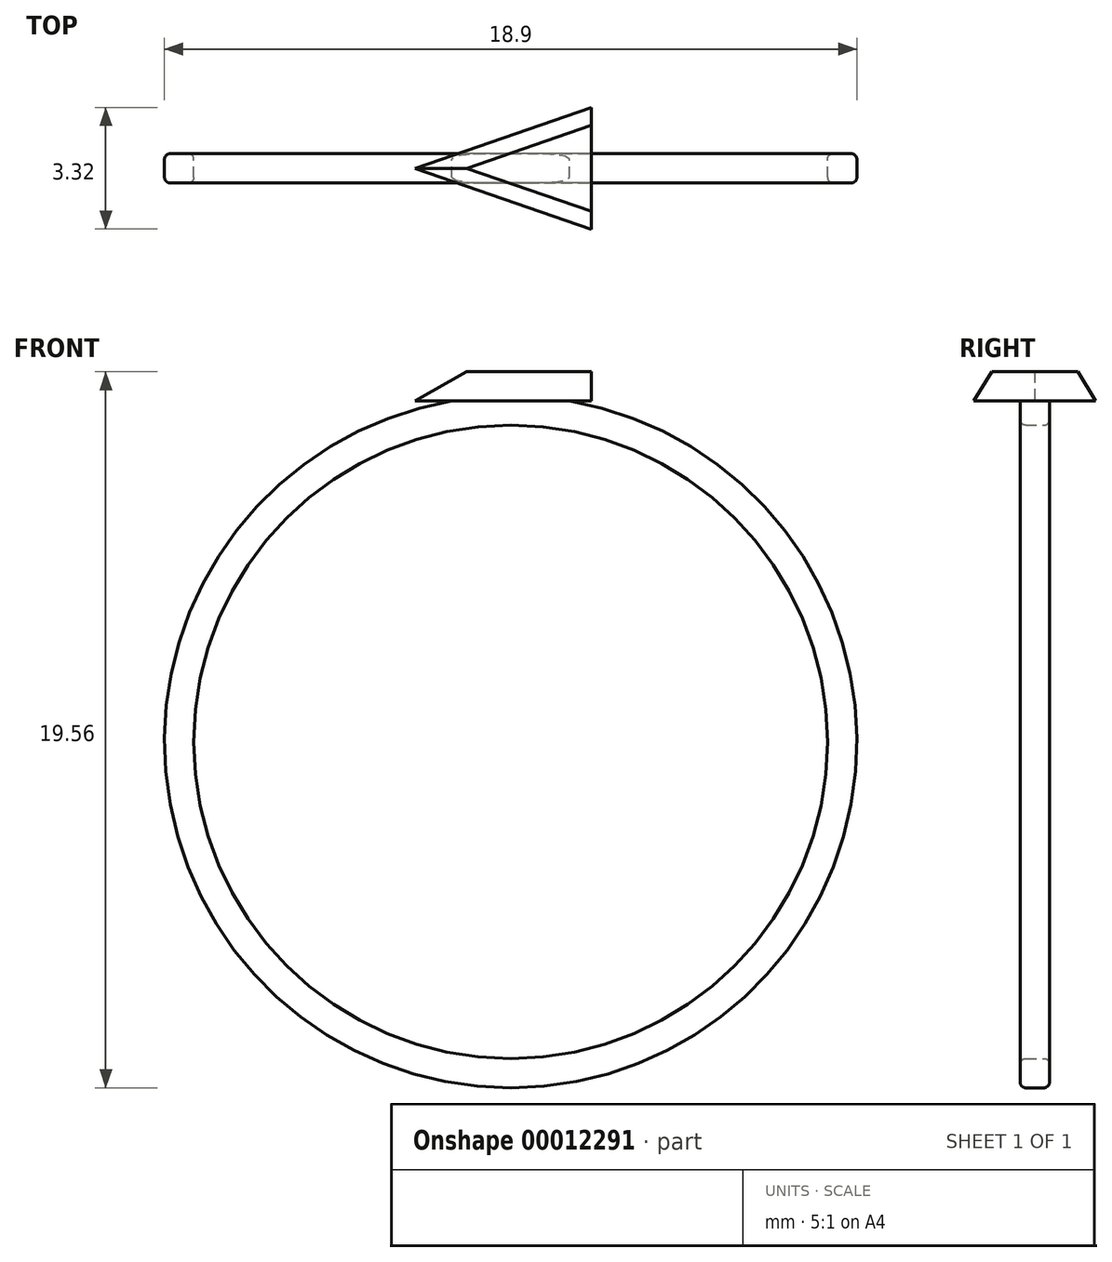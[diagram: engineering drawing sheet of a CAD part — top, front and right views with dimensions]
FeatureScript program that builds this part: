
annotation { "Feature Type Name" : "Feature", "Feature Type Description" : "" }
export const myFeature = defineFeature(function(context is Context, id is Id, definition is map)
    precondition{}
    {
        {
            var Q0;
            Q0=qCreatedBy(makeId("Front.planeOp"),FACE);
            var sketch = newSketch(context, id + "F0", { "sketchPlane" : qUnion([Q0])});
            skCircle(sketch, "E0", {"center": v(0, 0) * mm, "radius": 8.65 * mm});
            skCircle(sketch, "E1", {"center": v(0, 0) * mm, "radius": 9.45 * mm});
            skLineSegment(sketch, "E2", {"start": v(-1.6, 9.31) * mm, "end": v(1.6, 9.31) * mm});
            skLineSegment(sketch, "E3", {"start": v(1.6, 9.31) * mm, "end": v(0, 0) * mm});
            skLineSegment(sketch, "E4", {"start": v(-1.6, 9.31) * mm, "end": v(0, 0) * mm});
            skSolve(sketch);
        }
        {
            var Q0;
            {var subQ1=sQuery(id+"F0.wireOp",EDGE,"E0");var subQ6=sQuery(id+"F0.wireOp",EDGE,"E3");var subQ7=makeQuery(id+"F0.imprint","INTERSECT",VERTEX,{"derivedFrom":[subQ1,subQ6]});Q0=makeQuery(id+"F0.imprint","IMPRINT",FACE,{"disambiguationData":[TD([[makeQuery(id+"F0.imprint","IMPRINT",EDGE,{"disambiguationData":[TD([[subQ7,1.0]])],"derivedFrom":subQ1}),-1.0]])]});}
            var Q1;
            {var subQ4=sQuery(id+"F0.wireOp",EDGE,"E2");Q1=makeQuery(id+"F0.imprint","IMPRINT",FACE,{"disambiguationData":[TD([[makeQuery(id+"F0.imprint","IMPRINT",EDGE,{"derivedFrom":subQ4}),-1.0]])]});}
            extrude(context, id + "F1", {"entities" : qUnion([Q0, Q1]), "depth" : .4 * mm});
        }
        {
            var Q0;
            {var subQ1=sQuery(id+"F0.wireOp",EDGE,"E0");var subQ6=sQuery(id+"F0.wireOp",EDGE,"E3");var subQ7=makeQuery(id+"F0.imprint","INTERSECT",VERTEX,{"derivedFrom":[subQ1,subQ6]});Q0=makeQuery(id+"F0.imprint","IMPRINT",FACE,{"disambiguationData":[TD([[makeQuery(id+"F0.imprint","IMPRINT",EDGE,{"disambiguationData":[TD([[subQ7,1.0]])],"derivedFrom":subQ1}),-1.0]])]});}
            var Q1;
            {var subQ4=sQuery(id+"F0.wireOp",EDGE,"E2");Q1=makeQuery(id+"F0.imprint","IMPRINT",FACE,{"disambiguationData":[TD([[makeQuery(id+"F0.imprint","IMPRINT",EDGE,{"derivedFrom":subQ4}),-1.0]])]});}
            extrude(context, id + "F2", {"entities" : qUnion([Q0, Q1]), "operationType" : NewBodyOperationType.ADD, "oppositeDirection" : true, "depth" : .4 * mm});
        }
        {
            var Q0;
            {var subQ0=sQuery(id+"F0.wireOp",EDGE,"E2");Q0=makeQuery(id+"F2.boolean.opBoolean","MERGE",FACE,{"derivedFrom":[makeQuery(id+"F1.opExtrude","SWEPT_FACE",FACE,{"disambiguationData":[OSD([subQ0])]}),makeQuery(id+"F2.opExtrude","SWEPT_FACE",FACE,{"disambiguationData":[OSD([subQ0])]})]});}
            var sketch = newSketch(context, id + "F3", { "sketchPlane" : qUnion([Q0])});
            skLineSegment(sketch, "E5", {"start": v(2.2, -1.66) * mm, "end": v(-2.6, 0) * mm});
            skLineSegment(sketch, "E6", {"start": v(-2.6, 0) * mm, "end": v(2.2, 1.66) * mm});
            skLineSegment(sketch, "E7", {"start": v(2.2, -1.66) * mm, "end": v(2.2, 1.66) * mm});
            skSolve(sketch);
        }
        {
            var Q0;
            Q0=makeQuery(id+"F2.opExtrude","CAP_EDGE",EDGE,{"disambiguationData":[OSD([sQuery(id+"F0.wireOp",EDGE,"E1")])],"isStart":false});
            var Q1;
            Q1=makeQuery(id+"F2.opExtrude","CAP_EDGE",EDGE,{"disambiguationData":[OSD([sQuery(id+"F0.wireOp",EDGE,"E0")])],"isStart":false});
            var Q2;
            Q2=makeQuery(id+"F1.opExtrude","CAP_EDGE",EDGE,{"disambiguationData":[OSD([sQuery(id+"F0.wireOp",EDGE,"E0")])],"isStart":false});
            var Q3;
            Q3=makeQuery(id+"F1.opExtrude","CAP_EDGE",EDGE,{"disambiguationData":[OSD([sQuery(id+"F0.wireOp",EDGE,"E1")])],"isStart":false});
            fillet(context, id + "F4", {"entities" : qUnion([Q0, Q1, Q2, Q3]), "radius" : .15 * mm, "tangentPropagation" : true, "allowEdgeOverflow" : false});
        }
        {
            var Q0;
            Q0=qSketchRegion(id+"F3",true);
            extrude(context, id + "F5", {"entities" : qUnion([Q0]), "operationType" : NewBodyOperationType.ADD, "depth" : .8 * mm});
        }
        {
            var Q0;
            Q0=makeQuery(id+"F5.opExtrude","CAP_EDGE",EDGE,{"disambiguationData":[OSD([sQuery(id+"F3.wireOp",EDGE,"E5")])],"isStart":false});
            var Q1;
            Q1=makeQuery(id+"F5.opExtrude","CAP_EDGE",EDGE,{"disambiguationData":[OSD([sQuery(id+"F3.wireOp",EDGE,"E6")])],"isStart":false});
            chamfer(context, id + "F6", {"entities" : qUnion([Q0, Q1]), "chamferType" : ChamferType.OFFSET_ANGLE, "width" : .8 * mm, "oppositeDirection" : false, "angle" : 30 * degree, "tangentPropagation" : true});
        }
    });
